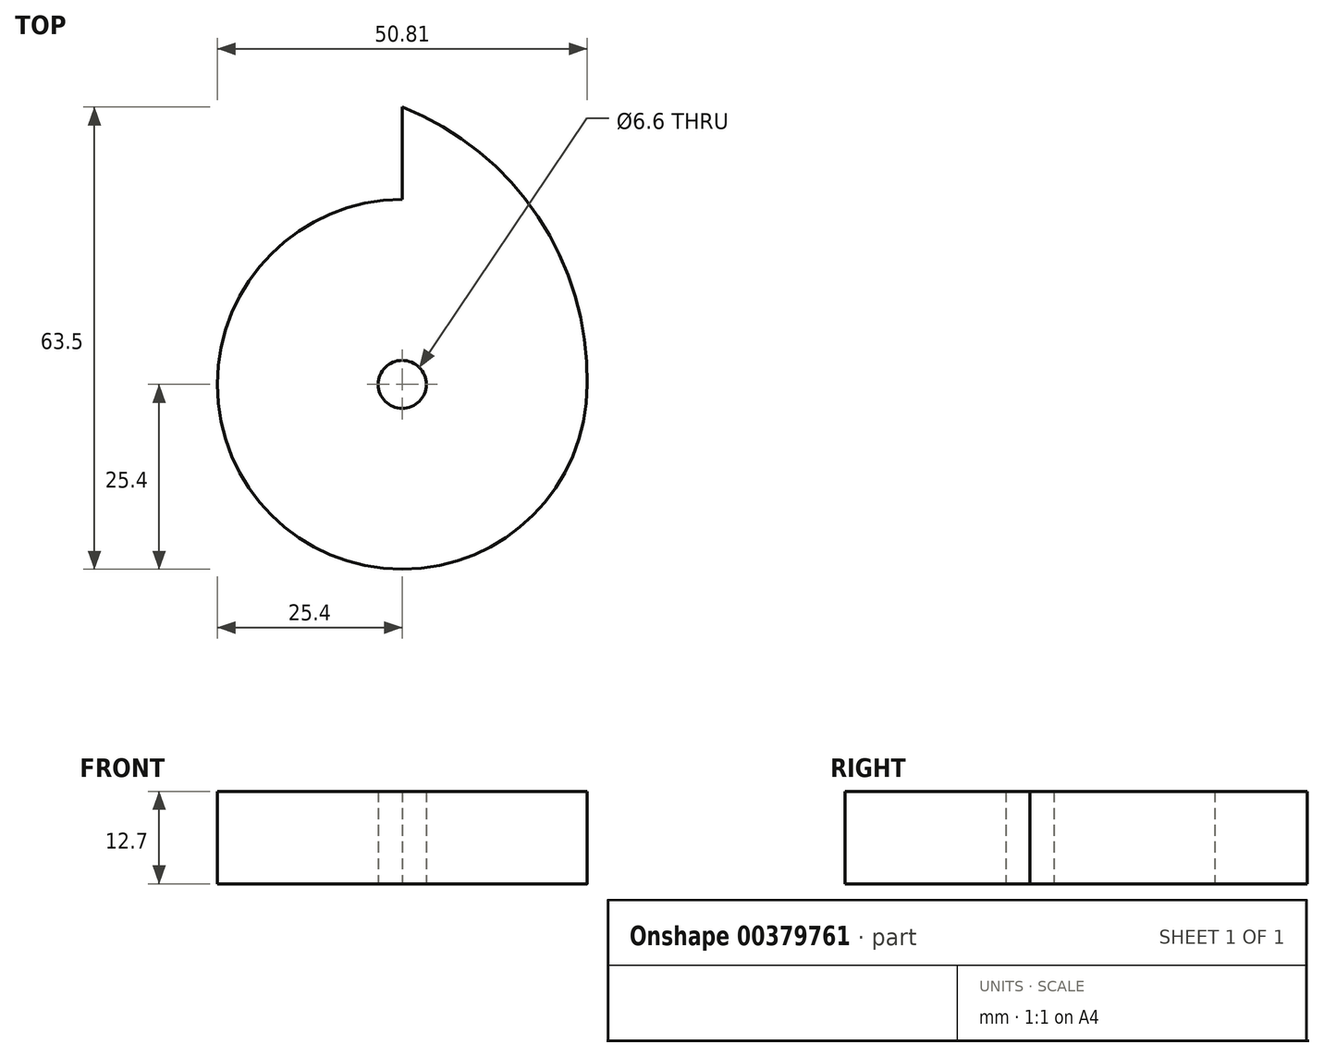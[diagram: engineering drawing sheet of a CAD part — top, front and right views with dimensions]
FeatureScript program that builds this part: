
annotation { "Feature Type Name" : "Feature", "Feature Type Description" : "" }
export const myFeature = defineFeature(function(context is Context, id is Id, definition is map)
    precondition{}
    {
        {
            var Q0;
            Q0=qCreatedBy(makeId("Top.planeOp"),FACE);
            var sketch = newSketch(context, id + "F0", { "sketchPlane" : qUnion([Q0])});
            skCircle(sketch, "E0", {"center": v(0, 0) * mm, "radius": 25.4 * mm});
            skLineSegment(sketch, "E1", {"start": v(0, 25.4) * mm, "end": v(0, 38.1) * mm});
            skArc(sketch, "E2", {"start": v(25.4, 0) * mm, "mid": v(18.67, 23.03) * mm, "end": v(0, 38.1) * mm});
            skCircle(sketch, "E3", {"center": v(0, 0) * mm, "radius": 3.3 * mm});
            skSolve(sketch);
        }
        {
            var Q0;
            {var subQ0=sQuery(id+"F0.wireOp",EDGE,"E1");Q0=makeQuery(id+"F0.imprint","IMPRINT",FACE,{"disambiguationData":[TD([[makeQuery(id+"F0.imprint","IMPRINT",EDGE,{"derivedFrom":subQ0}),-1.0]])]});}
            var Q1;
            {var subQ0=sQuery(id+"F0.wireOp",EDGE,"E0");var subQ1=makeQuery(id+"F0.imprint","INTERSECT",VERTEX,{"derivedFrom":[subQ0,sQuery(id+"F0.wireOp",EDGE,"E1")]});Q1=makeQuery(id+"F0.imprint","IMPRINT",FACE,{"disambiguationData":[TD([[makeQuery(id+"F0.imprint","IMPRINT",EDGE,{"disambiguationData":[TD([[subQ1,1.0]])],"derivedFrom":subQ0}),1.0]])]});}
            extrude(context, id + "F1", {"entities" : qUnion([Q0, Q1]), "depth" : 12.7 * mm});
        }
    });
